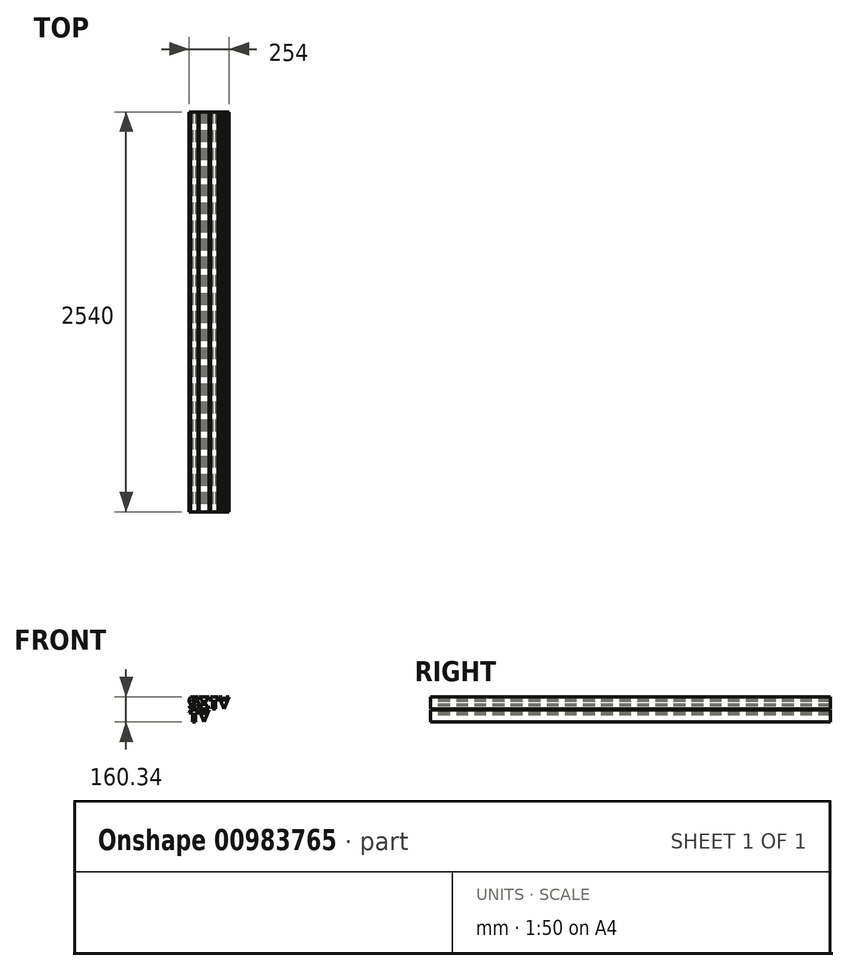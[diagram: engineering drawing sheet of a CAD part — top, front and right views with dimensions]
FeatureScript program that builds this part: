
annotation { "Feature Type Name" : "Feature", "Feature Type Description" : "" }
export const myFeature = defineFeature(function(context is Context, id is Id, definition is map)
    precondition{}
    {
        {
            var Q0;
            Q0=qCreatedBy(makeId("Front.planeOp"),FACE);
            var sketch = newSketch(context, id + "F0", { "sketchPlane" : qUnion([Q0])});
            skLineSegment(sketch, "E0", {"start": v(0, 76.2) * mm, "end": v(-7.94, 76.2) * mm, "construction": true});
            skLineSegment(sketch, "E1", {"start": v(-7.94, 76.2) * mm, "end": v(-55.56, 76.2) * mm});
            skLineSegment(sketch, "E2", {"start": v(-55.56, 76.2) * mm, "end": v(-63.5, 76.2) * mm, "construction": true});
            skLineSegment(sketch, "E3", {"start": v(0, 0) * mm, "end": v(0, 19.05) * mm, "construction": true});
            skLineSegment(sketch, "E4", {"start": v(0, 19.05) * mm, "end": v(0, 28.58) * mm});
            skLineSegment(sketch, "E5", {"start": v(0, 28.58) * mm, "end": v(0, 47.62) * mm, "construction": true});
            skLineSegment(sketch, "E6", {"start": v(0, 47.62) * mm, "end": v(0, 57.15) * mm, "construction": true});
            skLineSegment(sketch, "E7", {"start": v(0, 57.15) * mm, "end": v(0, 76.2) * mm, "construction": true});
            skLineSegment(sketch, "E8", {"start": v(-7.94, 76.2) * mm, "end": v(0, 57.15) * mm});
            skLineSegment(sketch, "E9", {"start": v(0, 0) * mm, "end": v(-7.94, 0) * mm, "construction": true});
            skLineSegment(sketch, "E10", {"start": v(-7.94, 0) * mm, "end": v(-55.56, 0) * mm});
            skLineSegment(sketch, "E11", {"start": v(-55.56, 0) * mm, "end": v(-63.5, 0) * mm, "construction": true});
            skLineSegment(sketch, "E12", {"start": v(-63.5, 76.2) * mm, "end": v(-63.5, 57.15) * mm, "construction": true});
            skLineSegment(sketch, "E13", {"start": v(-63.5, 57.15) * mm, "end": v(-63.5, 47.62) * mm});
            skLineSegment(sketch, "E14", {"start": v(-63.5, 47.62) * mm, "end": v(-63.5, 28.57) * mm, "construction": true});
            skLineSegment(sketch, "E15", {"start": v(-63.5, 28.57) * mm, "end": v(-63.5, 19.05) * mm, "construction": true});
            skLineSegment(sketch, "E16", {"start": v(-63.5, 19.05) * mm, "end": v(-63.5, 0) * mm, "construction": true});
            skLineSegment(sketch, "E17", {"start": v(-63.5, 19.05) * mm, "end": v(-55.56, 0) * mm});
            skLineSegment(sketch, "E18", {"start": v(0, 19.05) * mm, "end": v(-7.94, 0) * mm});
            skLineSegment(sketch, "E19", {"start": v(-55.56, 76.2) * mm, "end": v(-63.5, 57.15) * mm});
            skLineSegment(sketch, "E20", {"start": v(0, 47.62) * mm, "end": v(-7.94, 47.62) * mm, "construction": true});
            skLineSegment(sketch, "E21", {"start": v(-7.94, 47.63) * mm, "end": v(0, 28.57) * mm});
            skLineSegment(sketch, "E22", {"start": v(-63.5, 28.57) * mm, "end": v(-55.56, 28.58) * mm, "construction": true});
            skLineSegment(sketch, "E23", {"start": v(-55.56, 28.58) * mm, "end": v(-63.5, 47.62) * mm});
            skLineSegment(sketch, "E24", {"start": v(-63.5, 19.05) * mm, "end": v(-19.05, 19.05) * mm});
            skLineSegment(sketch, "E25", {"start": v(-19.05, 19.05) * mm, "end": v(-19.05, 28.58) * mm});
            skLineSegment(sketch, "E26", {"start": v(-19.05, 28.58) * mm, "end": v(-55.56, 28.58) * mm});
            skLineSegment(sketch, "E27", {"start": v(0, 57.15) * mm, "end": v(-44.45, 57.15) * mm});
            skLineSegment(sketch, "E28", {"start": v(-44.45, 57.15) * mm, "end": v(-44.45, 47.62) * mm});
            skLineSegment(sketch, "E29", {"start": v(-44.45, 47.62) * mm, "end": v(-7.94, 47.63) * mm});
            skLineSegment(sketch, "E30", {"start": v(0, 0) * mm, "end": v(7.94, 19.05) * mm});
            skLineSegment(sketch, "E31", {"start": v(7.94, 19.05) * mm, "end": v(22.22, 19.05) * mm});
            skLineSegment(sketch, "E32", {"start": v(22.22, 19.05) * mm, "end": v(22.22, 57.15) * mm});
            skLineSegment(sketch, "E33", {"start": v(22.22, 57.15) * mm, "end": v(7.94, 57.15) * mm});
            skLineSegment(sketch, "E34", {"start": v(7.94, 57.15) * mm, "end": v(0, 76.2) * mm});
            skLineSegment(sketch, "E35", {"start": v(0, 76.2) * mm, "end": v(63.5, 76.2) * mm});
            skLineSegment(sketch, "E36", {"start": v(63.5, 76.2) * mm, "end": v(55.56, 57.15) * mm});
            skLineSegment(sketch, "E37", {"start": v(55.56, 57.15) * mm, "end": v(41.27, 57.15) * mm});
            skLineSegment(sketch, "E38", {"start": v(41.27, 57.15) * mm, "end": v(41.27, 19.05) * mm});
            skLineSegment(sketch, "E39", {"start": v(41.27, 19.05) * mm, "end": v(55.56, 19.05) * mm});
            skLineSegment(sketch, "E40", {"start": v(55.56, 19.05) * mm, "end": v(63.5, 0) * mm});
            skLineSegment(sketch, "E41", {"start": v(41.27, 19.05) * mm, "end": v(22.22, 19.05) * mm, "construction": true});
            skLineSegment(sketch, "E42", {"start": v(22.22, 0) * mm, "end": v(22.22, 19.05) * mm, "construction": true});
            skLineSegment(sketch, "E43", {"start": v(22.22, 57.15) * mm, "end": v(41.27, 57.15) * mm, "construction": true});
            skLineSegment(sketch, "E44", {"start": v(22.22, 57.15) * mm, "end": v(22.22, 76.2) * mm, "construction": true});
            skLineSegment(sketch, "E45", {"start": v(0, 0) * mm, "end": v(63.5, 0) * mm});
            skLineSegment(sketch, "E46", {"start": v(0, 0) * mm, "end": v(0, -7.94) * mm, "construction": true});
            skLineSegment(sketch, "E47", {"start": v(0, -7.94) * mm, "end": v(-7.94, -7.94) * mm, "construction": true});
            skLineSegment(sketch, "E48", {"start": v(-7.94, 0) * mm, "end": v(-7.94, -7.94) * mm, "construction": true});
            skLineSegment(sketch, "E49", {"start": v(-7.94, -7.94) * mm, "end": v(-55.56, -7.94) * mm});
            skLineSegment(sketch, "E50", {"start": v(-55.56, -7.94) * mm, "end": v(-55.56, 0) * mm, "construction": true});
            skLineSegment(sketch, "E51", {"start": v(-63.5, 0) * mm, "end": v(-63.5, -7.94) * mm, "construction": true});
            skLineSegment(sketch, "E52", {"start": v(-63.5, -7.94) * mm, "end": v(-55.56, -7.94) * mm, "construction": true});
            skLineSegment(sketch, "E53", {"start": v(-63.5, -7.94) * mm, "end": v(-63.5, -26.99) * mm, "construction": true});
            skLineSegment(sketch, "E54", {"start": v(-63.5, -26.99) * mm, "end": v(-55.56, -7.94) * mm});
            skLineSegment(sketch, "E55", {"start": v(-7.94, -7.94) * mm, "end": v(0, -26.99) * mm});
            skLineSegment(sketch, "E56", {"start": v(0, -26.99) * mm, "end": v(-22.23, -26.99) * mm});
            skLineSegment(sketch, "E57", {"start": v(-22.23, -26.99) * mm, "end": v(-22.22, -84.14) * mm});
            skLineSegment(sketch, "E58", {"start": v(-22.22, -84.14) * mm, "end": v(-41.27, -84.14) * mm});
            skLineSegment(sketch, "E59", {"start": v(-41.27, -84.14) * mm, "end": v(-41.27, -26.99) * mm});
            skLineSegment(sketch, "E60", {"start": v(-41.27, -26.99) * mm, "end": v(-63.5, -26.99) * mm});
            skLineSegment(sketch, "E61", {"start": v(0, -7.94) * mm, "end": v(0, -26.99) * mm, "construction": true});
            skLineSegment(sketch, "E62", {"start": v(-22.23, -26.99) * mm, "end": v(-41.27, -26.99) * mm, "construction": true});
            skLineSegment(sketch, "E63", {"start": v(0, -7.94) * mm, "end": v(31.75, -84.14) * mm});
            skLineSegment(sketch, "E64", {"start": v(31.75, -84.14) * mm, "end": v(63.5, -7.94) * mm});
            skLineSegment(sketch, "E65", {"start": v(63.5, -7.94) * mm, "end": v(44.45, -7.94) * mm});
            skLineSegment(sketch, "E66", {"start": v(44.45, -7.94) * mm, "end": v(19.05, -7.94) * mm, "construction": true});
            skLineSegment(sketch, "E67", {"start": v(19.05, -7.94) * mm, "end": v(0, -7.94) * mm});
            skLineSegment(sketch, "E68", {"start": v(31.75, -7.94) * mm, "end": v(31.75, -84.14) * mm, "construction": true});
            skLineSegment(sketch, "E69", {"start": v(19.05, -7.94) * mm, "end": v(31.75, -38.42) * mm});
            skLineSegment(sketch, "E70", {"start": v(31.75, -38.42) * mm, "end": v(44.45, -7.94) * mm});
            skLineSegment(sketch, "E71", {"start": v(63.5, 76.2) * mm, "end": v(63.5, 57.15) * mm, "construction": true});
            skLineSegment(sketch, "E72", {"start": v(63.5, 57.15) * mm, "end": v(55.56, 57.15) * mm, "construction": true});
            skLineSegment(sketch, "E73", {"start": v(63.5, 57.15) * mm, "end": v(71.44, 76.2) * mm});
            skLineSegment(sketch, "E74", {"start": v(71.44, 76.2) * mm, "end": v(119.06, 76.2) * mm});
            skLineSegment(sketch, "E75", {"start": v(119.06, 76.2) * mm, "end": v(127, 57.15) * mm});
            skLineSegment(sketch, "E76", {"start": v(127, 57.15) * mm, "end": v(104.77, 57.15) * mm});
            skLineSegment(sketch, "E77", {"start": v(104.77, 57.15) * mm, "end": v(104.77, 0) * mm});
            skLineSegment(sketch, "E78", {"start": v(104.77, 0) * mm, "end": v(85.72, 0) * mm});
            skLineSegment(sketch, "E79", {"start": v(85.72, 0) * mm, "end": v(85.72, 57.15) * mm});
            skLineSegment(sketch, "E80", {"start": v(85.72, 57.15) * mm, "end": v(63.5, 57.15) * mm});
            skLineSegment(sketch, "E81", {"start": v(104.77, 57.15) * mm, "end": v(85.72, 57.15) * mm, "construction": true});
            skLineSegment(sketch, "E82", {"start": v(127, 57.15) * mm, "end": v(127, 76.2) * mm, "construction": true});
            skLineSegment(sketch, "E83", {"start": v(127, 76.2) * mm, "end": v(119.06, 76.2) * mm, "construction": true});
            skLineSegment(sketch, "E84", {"start": v(127, 76.2) * mm, "end": v(146.05, 76.2) * mm});
            skLineSegment(sketch, "E85", {"start": v(146.05, 76.2) * mm, "end": v(171.45, 76.2) * mm, "construction": true});
            skLineSegment(sketch, "E86", {"start": v(171.45, 76.2) * mm, "end": v(190.5, 76.2) * mm});
            skLineSegment(sketch, "E87", {"start": v(190.5, 76.2) * mm, "end": v(158.75, 0) * mm});
            skLineSegment(sketch, "E88", {"start": v(158.75, 0) * mm, "end": v(127, 76.2) * mm});
            skLineSegment(sketch, "E89", {"start": v(158.75, 76.2) * mm, "end": v(158.75, 0) * mm, "construction": true});
            skLineSegment(sketch, "E90", {"start": v(146.05, 76.2) * mm, "end": v(158.75, 45.72) * mm});
            skLineSegment(sketch, "E91", {"start": v(158.75, 45.72) * mm, "end": v(171.45, 76.2) * mm});
            skSolve(sketch);
        }
        {
            var Q0;
            Q0=qSketchRegion(id+"F0",true);
            extrude(context, id + "F1", {"entities" : qUnion([Q0]), "oppositeDirection" : true, "depth" : 2540 * mm, "offsetDistance" : 25.4 * mm});
        }
    });
